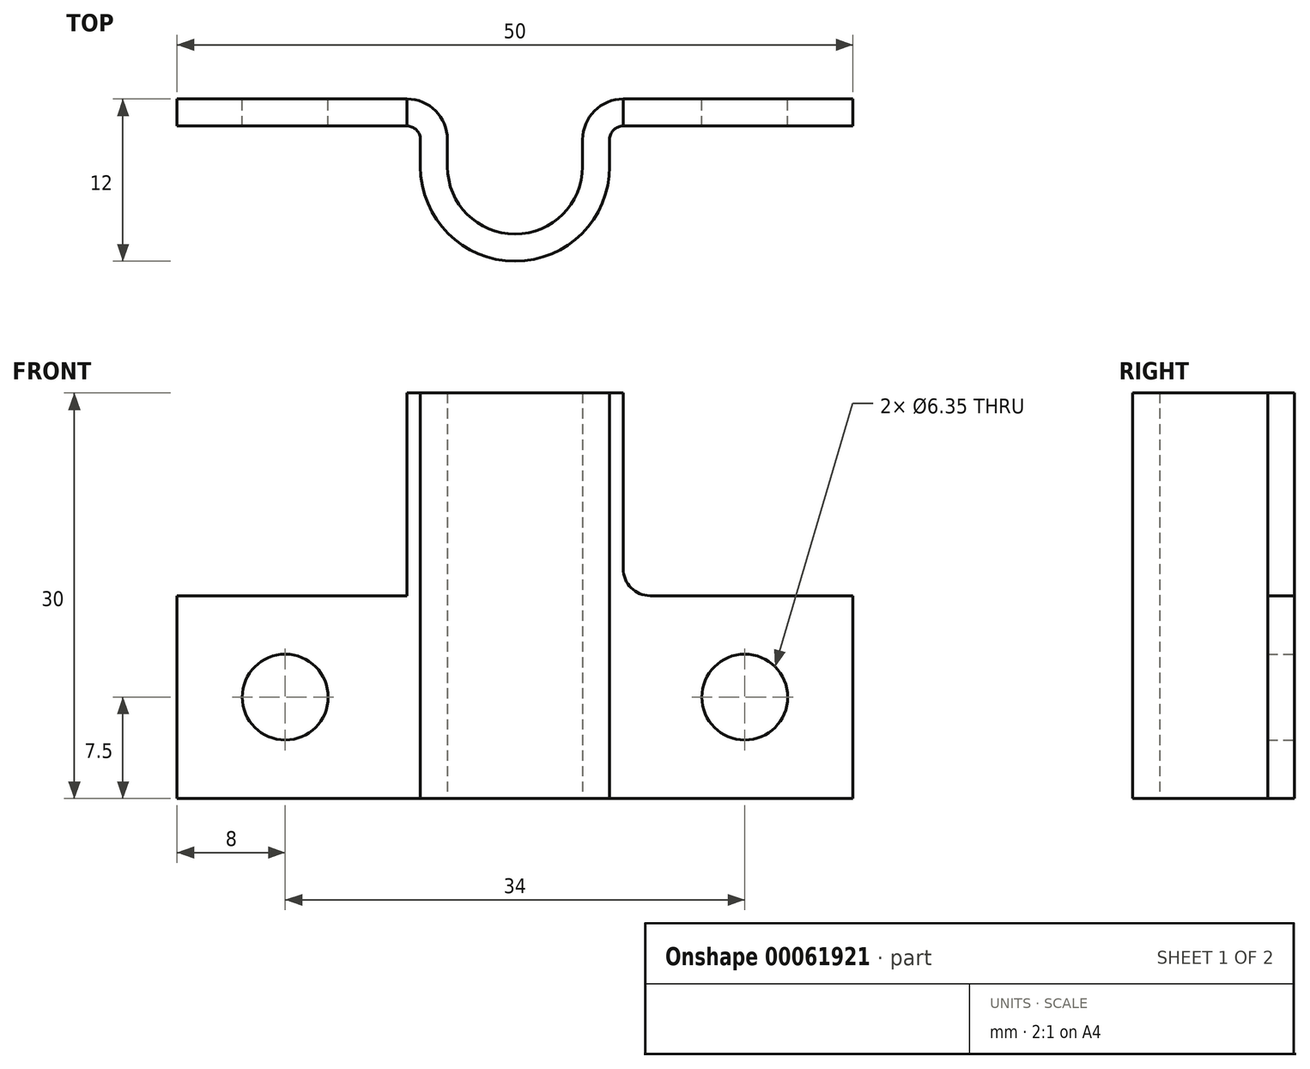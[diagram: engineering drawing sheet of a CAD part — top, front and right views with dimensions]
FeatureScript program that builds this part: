
annotation { "Feature Type Name" : "Feature", "Feature Type Description" : "" }
export const myFeature = defineFeature(function(context is Context, id is Id, definition is map)
    precondition{}
    {
        {
            var Q0;
            Q0=qCreatedBy(makeId("Top.planeOp"),FACE);
            var sketch = newSketch(context, id + "F0", { "sketchPlane" : qUnion([Q0])});
            skLineSegment(sketch, "E0", {"start": v(-25, 0) * mm, "end": v(-8, 0) * mm});
            skLineSegment(sketch, "E1", {"start": v(8, 0) * mm, "end": v(25, 0) * mm});
            skArc(sketch, "E2", {"start": v(-5, -5) * mm, "mid": v(0, -10) * mm, "end": v(5, -5) * mm});
            skLineSegment(sketch, "E3", {"start": v(-5, -5) * mm, "end": v(-5, -3) * mm});
            skLineSegment(sketch, "E4", {"start": v(5, -5) * mm, "end": v(5, -3) * mm});
            skPoint(sketch, "E5.visualSharp", {"position": v(-5, 0) * mm});
            skArc(sketch, "E5.filletArc", {"start": v(-5, -3) * mm, "mid": v(-5.88, -0.88) * mm, "end": v(-8, 0) * mm});
            skPoint(sketch, "E6.visualSharp", {"position": v(5, 0) * mm});
            skArc(sketch, "E6.filletArc", {"start": v(8, 0) * mm, "mid": v(5.88, -0.88) * mm, "end": v(5, -3) * mm});
            skLineSegment(sketch, "E7.0", {"start": v(-25, -2) * mm, "end": v(-8, -2) * mm});
            skArc(sketch, "E8.0", {"start": v(-7, -5) * mm, "mid": v(0, -12) * mm, "end": v(7, -5) * mm});
            skLineSegment(sketch, "E9.0", {"start": v(-7, -5) * mm, "end": v(-7, -3) * mm});
            skLineSegment(sketch, "E10.0", {"start": v(8, -2) * mm, "end": v(25, -2) * mm});
            skLineSegment(sketch, "E11.0", {"start": v(7, -5) * mm, "end": v(7, -3) * mm});
            skArc(sketch, "E12.filletArc", {"start": v(-7, -3) * mm, "mid": v(-7.3, -2.3) * mm, "end": v(-8, -2) * mm});
            skArc(sketch, "E13.filletArc", {"start": v(8, -2) * mm, "mid": v(7.3, -2.3) * mm, "end": v(7, -3) * mm});
            skLineSegment(sketch, "E14", {"start": v(-25, 0) * mm, "end": v(-25, -2) * mm});
            skLineSegment(sketch, "E15", {"start": v(25, 0) * mm, "end": v(25, -2) * mm});
            skSolve(sketch);
        }
        {
            var Q0;
            Q0=makeQuery(id+"F0.imprint","IMPRINT",FACE,{"disambiguationData":[TD([[makeQuery(id+"F0.imprint","IMPRINT",EDGE,{"derivedFrom":sQuery(id+"F0.wireOp",EDGE,"E0")}),-1.0]])]});
            extrude(context, id + "F1", {"entities" : qUnion([Q0]), "depth" : 15 * mm});
        }
        {
            var Q0;
            Q0=makeQuery(id+"F1.opExtrude","CAP_FACE",FACE,{"disambiguationData":[OSD([sQuery(id+"F0.wireOp",EDGE,"E0"),sQuery(id+"F0.wireOp",EDGE,"E1"),sQuery(id+"F0.wireOp",EDGE,"E2"),sQuery(id+"F0.wireOp",EDGE,"E3"),sQuery(id+"F0.wireOp",EDGE,"E4"),sQuery(id+"F0.wireOp",EDGE,"E5.filletArc"),sQuery(id+"F0.wireOp",EDGE,"E6.filletArc"),sQuery(id+"F0.wireOp",EDGE,"E7.0"),sQuery(id+"F0.wireOp",EDGE,"E8.0"),sQuery(id+"F0.wireOp",EDGE,"E9.0"),sQuery(id+"F0.wireOp",EDGE,"E10.0"),sQuery(id+"F0.wireOp",EDGE,"E11.0"),sQuery(id+"F0.wireOp",EDGE,"E12.filletArc"),sQuery(id+"F0.wireOp",EDGE,"E13.filletArc"),sQuery(id+"F0.wireOp",EDGE,"E14"),sQuery(id+"F0.wireOp",EDGE,"E15")])],"isStart":false});
            var sketch = newSketch(context, id + "F2", { "sketchPlane" : qUnion([Q0])});
            skArc(sketch, "E16.0", {"start": v(-5, -3) * mm, "mid": v(-5.88, -0.88) * mm, "end": v(-8, 0) * mm});
            skLineSegment(sketch, "E17.0", {"start": v(-5, -5) * mm, "end": v(-5, -3) * mm});
            skArc(sketch, "E18.0", {"start": v(-5, -5) * mm, "mid": v(0, -10) * mm, "end": v(5, -5) * mm});
            skLineSegment(sketch, "E19.0", {"start": v(5, -5) * mm, "end": v(5, -3) * mm});
            skArc(sketch, "E20.0", {"start": v(8, 0) * mm, "mid": v(5.88, -0.88) * mm, "end": v(5, -3) * mm});
            skLineSegment(sketch, "E21.0", {"start": v(7, -5) * mm, "end": v(7, -3) * mm});
            skArc(sketch, "E22.0", {"start": v(8, -2) * mm, "mid": v(7.3, -2.3) * mm, "end": v(7, -3) * mm});
            skArc(sketch, "E23.0", {"start": v(-7, -5) * mm, "mid": v(0, -12) * mm, "end": v(7, -5) * mm});
            skLineSegment(sketch, "E24.0", {"start": v(-7, -5) * mm, "end": v(-7, -3) * mm});
            skArc(sketch, "E25.0", {"start": v(-7, -3) * mm, "mid": v(-7.3, -2.3) * mm, "end": v(-8, -2) * mm});
            skLineSegment(sketch, "E26", {"start": v(-8, 0) * mm, "end": v(-8, -2) * mm});
            skLineSegment(sketch, "E27", {"start": v(8, 0) * mm, "end": v(8, -2) * mm});
            skSolve(sketch);
        }
        {
            var Q0;
            Q0=makeQuery(id+"F2.imprint","IMPRINT",FACE,{"disambiguationData":[TD([[makeQuery(id+"F2.imprint","IMPRINT",EDGE,{"derivedFrom":sQuery(id+"F2.wireOp",EDGE,"E16.0")}),1.0]])]});
            extrude(context, id + "F3", {"entities" : qUnion([Q0]), "operationType" : NewBodyOperationType.ADD, "depth" : 15 * mm});
        }
        {
            var Q0;
            Q0=makeQuery(id+"F3.opExtrude","CAP_EDGE",EDGE,{"disambiguationData":[OSD([sQuery(id+"F2.wireOp",EDGE,"E26")])],"isStart":true});
            var Q1;
            Q1=makeQuery(id+"F3.opExtrude","CAP_EDGE",EDGE,{"disambiguationData":[OSD([sQuery(id+"F2.wireOp",EDGE,"E27")])],"isStart":true});
            fillet(context, id + "F4", {"entities" : qUnion([Q0, Q1]), "radius" : 2 * mm, "tangentPropagation" : true, "allowEdgeOverflow" : false});
        }
        {
            var Q0;
            Q0=makeQuery(id+"F1.opExtrude","SWEPT_FACE",FACE,{"disambiguationData":[OSD([sQuery(id+"F0.wireOp",EDGE,"E0")])]});
            var sketch = newSketch(context, id + "F5", { "sketchPlane" : qUnion([Q0])});
            skLineSegment(sketch, "E28", {"start": v(25, 7.5) * mm, "end": v(17, 7.5) * mm});
            skLineSegment(sketch, "E29.0", {"start": v(-25, 15) * mm, "end": v(-25, 0) * mm});
            skLineSegment(sketch, "E30", {"start": v(-25, 7.5) * mm, "end": v(-17, 7.5) * mm});
            skPoint(sketch, "E30.endSnap0", {"position": v(-25, 7.5) * mm});
            skSolve(sketch);
        }
        {
            var Q0;
            Q0=sQuery(id+"F5.wireOp",VERTEX,"E30.end");
            var Q1;
            Q1=sQuery(id+"F5.wireOp",VERTEX,"E28.end");
            var Q2;
            Q2=makeQuery(id+"F1.opExtrude","SWEPT_BODY",BODY,{"disambiguationData":[OSD([sQuery(id+"F0.wireOp",EDGE,"E0"),sQuery(id+"F0.wireOp",EDGE,"E1"),sQuery(id+"F0.wireOp",EDGE,"E2"),sQuery(id+"F0.wireOp",EDGE,"E3"),sQuery(id+"F0.wireOp",EDGE,"E4"),sQuery(id+"F0.wireOp",EDGE,"E5.filletArc"),sQuery(id+"F0.wireOp",EDGE,"E6.filletArc"),sQuery(id+"F0.wireOp",EDGE,"E7.0"),sQuery(id+"F0.wireOp",EDGE,"E8.0"),sQuery(id+"F0.wireOp",EDGE,"E9.0"),sQuery(id+"F0.wireOp",EDGE,"E10.0"),sQuery(id+"F0.wireOp",EDGE,"E11.0"),sQuery(id+"F0.wireOp",EDGE,"E12.filletArc"),sQuery(id+"F0.wireOp",EDGE,"E13.filletArc"),sQuery(id+"F0.wireOp",EDGE,"E14"),sQuery(id+"F0.wireOp",EDGE,"E15")])]});
            hole(context, id + "F6", {"style" : HoleStyle.SIMPLE, "holeDiameter" : 6.35 * mm, "endStyle" : HoleEndStyle.THROUGH, "locations" : qUnion([Q0, Q1]), "scope" : qUnion([Q2])});
        }
    });
